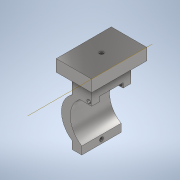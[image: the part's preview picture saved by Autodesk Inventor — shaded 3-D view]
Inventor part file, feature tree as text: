
AUTODESK INVENTOR PART (.ipt)
format: ipt  version: 2021 (Build 250183000, 183)  size: 215,040 bytes
history: native  units: in
note: dims shown in document units (in); Inventor stores cm internally (conversion verified against a paired STEP export)
features: sketch x7, extrude x5, hole x2, plane x1
ambient origin geometry x8: Origin, YZ Plane, XZ Plane, XY Plane, X Axis, Y Axis, Z Axis, Center Point
bodies: Solid1 (feature_tree)
feature tree (15):
  extrude  "Extrusion1"  Depth=3.937in TaperAngle=0.0deg
  extrude  "Extrusion6"  Depth=3.937in
  extrude  "Extrusion7"  Depth=2.3622in
  hole  "Hole3"  [1 undecoded]
  extrude  "Extrusion8"  Depth=3.937in TaperAngle=0.0deg
  extrude  "Extrusion9"  Depth=1.9685in
  hole  "Hole4"  [1 undecoded]
  plane  "Work Plane1"
  sketch  "Sketch2"  dims[d1=1.9685in d2=3.937in d3=0.0in]
  sketch  "Sketch12"  dims[d55=0.9843in d56=3.937in]
  sketch  "Sketch13"  dims[d57=1.9685in d58=2.3622in]
  sketch  "Sketch16"  dims[d59=0.7874in d60=2.3622in]
  sketch  "Sketch17"  dims[d61=0.7874in d62=3.937in d63=0.0in]
  sketch  "Sketch18"  dims[d68=0.9843in d69=1.9685in]
  sketch  "Sketch19"  dims[d70=5.5118in d71=3.5433in d72=1.1811in d73=0.0in d74=0.3937in d75=0.315in d76=0.2362in d77=0.3937in d78=0.1181in d79=90.0deg d80=0.315in d81=0.8108in d82=0.2756in d83=0.2756in d84=0.3937in d85=3.937in d86=0.0in d89=0.4724in d90=0.0in d91=0.3937in d92=0.3937in d93=0.3937in d94=0.2362in d95=0.3937in d96=0.1181in d97=90.0deg d98=0.315in d99=0.8108in d100=0.4724in d101=0.7874in d102=0.7874in d103=0.4724in d104=2.3622in d105=0.7874in d64=0.0197in d65=0.0344in d66=0.0197in d67=0.0344in]
note: 2 required parameter values undecoded (feature->parameter linkage not recoverable at this tier; creation-order binding heuristic only, values carry confidence <= 0.55)
